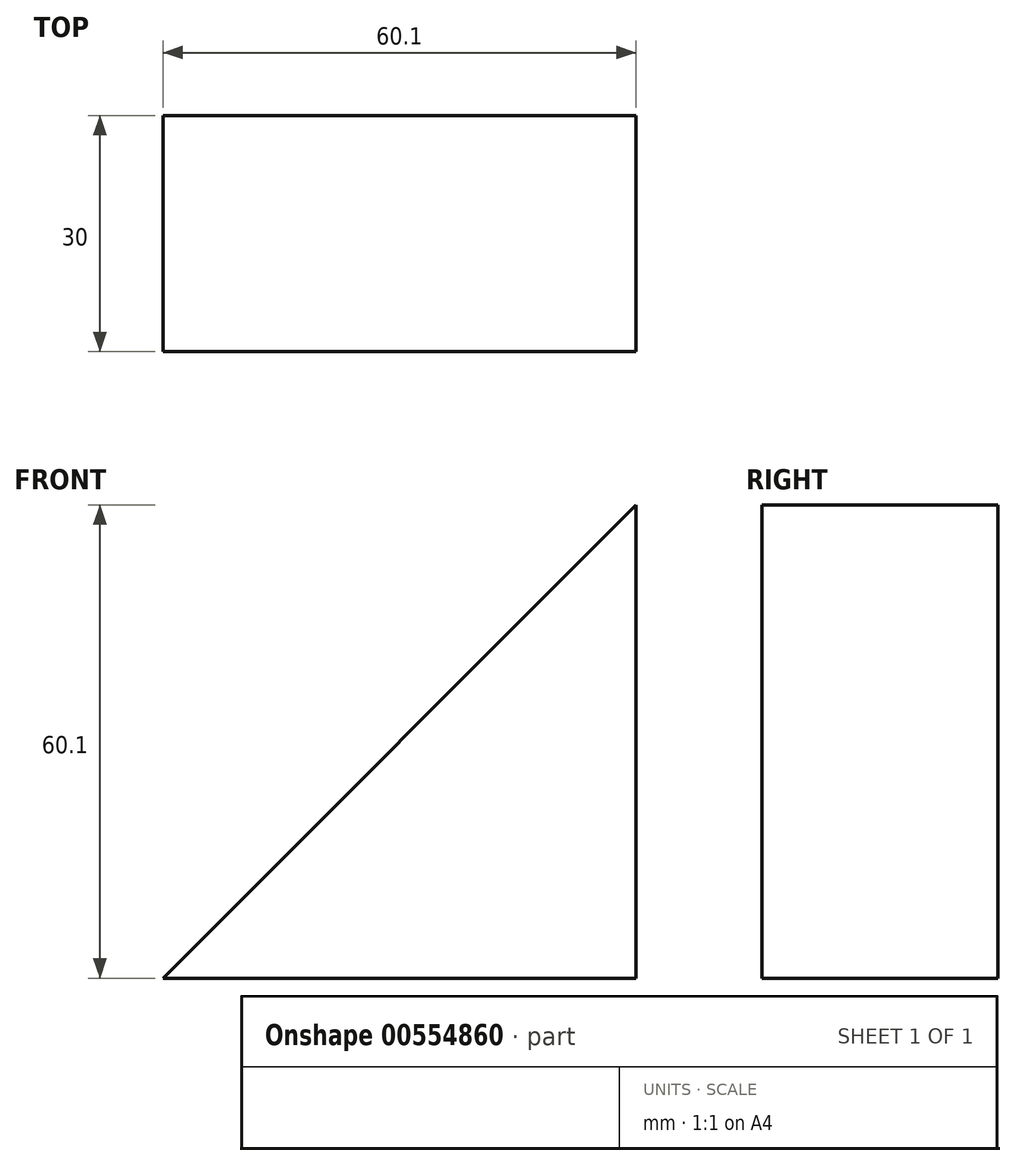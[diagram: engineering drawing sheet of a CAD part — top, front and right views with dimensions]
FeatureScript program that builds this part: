
annotation { "Feature Type Name" : "Feature", "Feature Type Description" : "" }
export const myFeature = defineFeature(function(context is Context, id is Id, definition is map)
    precondition{}
    {
        {
            var Q0;
            Q0=qCreatedBy(makeId("Front.planeOp"),FACE);
            var sketch = newSketch(context, id + "F0", { "sketchPlane" : qUnion([Q0])});
            skLineSegment(sketch, "E0.top", {"start": v(-24.85, -16.61) * mm, "end": v(35.25, -16.61) * mm});
            skLineSegment(sketch, "E0.right", {"start": v(35.25, 43.49) * mm, "end": v(35.25, -16.61) * mm});
            skLineSegment(sketch, "E1", {"start": v(-24.85, -16.61) * mm, "end": v(35.25, 43.49) * mm});
            skSolve(sketch);
        }
        {
            var Q0;
            Q0 = qSketchRegion(id + "F0", true);
            extrude(context, id + "F1", {"entities" : qUnion([Q0]), "depth" : 30 * mm, "offsetDistance" : 25 * mm});
        }
    });
